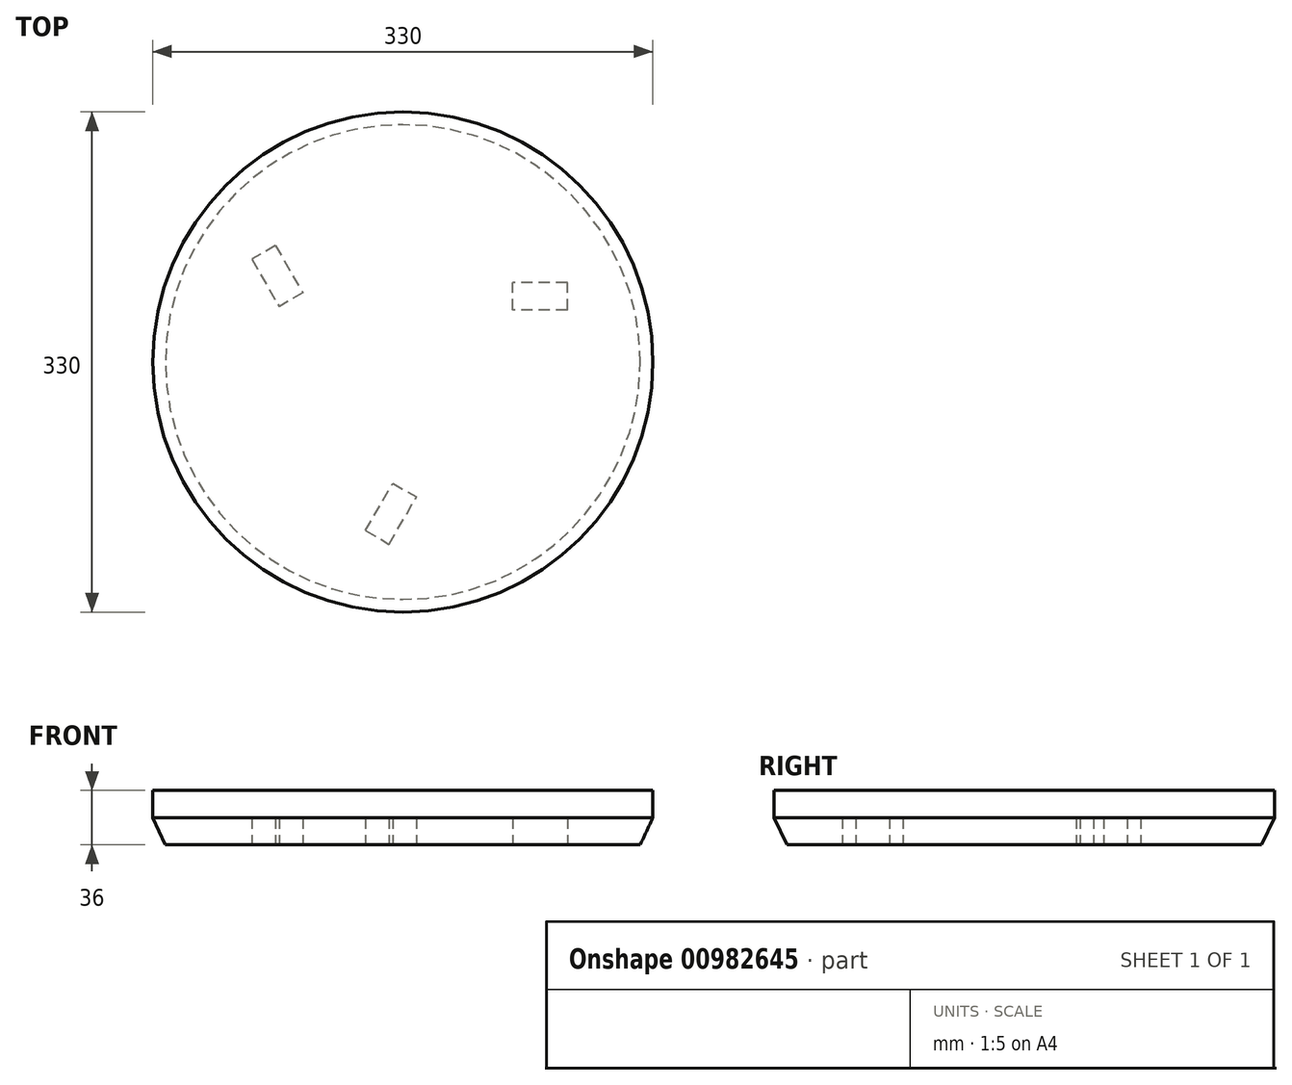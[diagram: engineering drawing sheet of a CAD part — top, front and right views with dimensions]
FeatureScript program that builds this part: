
annotation { "Feature Type Name" : "Feature", "Feature Type Description" : "" }
export const myFeature = defineFeature(function(context is Context, id is Id, definition is map)
    precondition{}
    {
        {
            var Q0;
            Q0=qCreatedBy(makeId("Top.planeOp"),FACE);
            var sketch = newSketch(context, id + "F0", { "sketchPlane" : qUnion([Q0])});
            skCircle(sketch, "E0", {"center": v(0, 0) * mm, "radius": 165 * mm});
            skSolve(sketch);
        }
        {
            var Q0;
            Q0=makeQuery(id+"F0.imprint","IMPRINT",FACE,{"disambiguationData":[TD([[makeQuery(id+"F0.imprint","IMPRINT",EDGE,{"derivedFrom":sQuery(id+"F0.wireOp",EDGE,"E0")}),1.0]])]});
            extrude(context, id + "F1", {"entities" : qUnion([Q0]), "depth" : 36 * mm, "offsetDistance" : 25 * mm});
        }
        {
            var Q0;
            Q0=makeQuery(id+"F1.opExtrude","CAP_FACE",FACE,{"disambiguationData":[OSD([sQuery(id+"F0.wireOp",EDGE,"E0")])],"isStart":true});
            var sketch = newSketch(context, id + "F2", { "sketchPlane" : qUnion([Q0])});
            skLineSegment(sketch, "E1.bottom", {"start": v(-24.59, 111.18) * mm, "end": v(-9, 120.18) * mm});
            skLineSegment(sketch, "E1.top", {"start": v(-6.59, 80) * mm, "end": v(9, 89) * mm});
            skLineSegment(sketch, "E1.left", {"start": v(-24.59, 111.18) * mm, "end": v(-6.59, 80) * mm});
            skLineSegment(sketch, "E1.right", {"start": v(-9, 120.18) * mm, "end": v(9, 89) * mm});
            skLineSegment(sketch, "E2", {"start": v(0, 0) * mm, "end": v(0, 83.8) * mm, "construction": true});
            skLineSegment(sketch, "E3.1.0", {"start": v(-99.58, -67.88) * mm, "end": v(-81.58, -36.7) * mm});
            skLineSegment(sketch, "E3.1.1", {"start": v(-83.99, -76.88) * mm, "end": v(-99.58, -67.88) * mm});
            skLineSegment(sketch, "E3.1.2", {"start": v(-83.99, -76.88) * mm, "end": v(-65.99, -45.7) * mm});
            skLineSegment(sketch, "E3.1.3", {"start": v(-65.99, -45.7) * mm, "end": v(-81.58, -36.7) * mm});
            skLineSegment(sketch, "E3.2.0", {"start": v(108.58, -52.3) * mm, "end": v(72.58, -52.3) * mm});
            skLineSegment(sketch, "E3.2.1", {"start": v(108.58, -34.3) * mm, "end": v(108.58, -52.3) * mm});
            skLineSegment(sketch, "E3.2.2", {"start": v(108.58, -34.3) * mm, "end": v(72.58, -34.3) * mm});
            skLineSegment(sketch, "E3.2.3", {"start": v(72.58, -34.3) * mm, "end": v(72.58, -52.3) * mm});
            skPoint(sketch, "E3.center", {"position": v(0, 0) * mm});
            skSolve(sketch);
        }
        {
            var Q0;
            Q0=makeQuery(id+"F2.imprint","IMPRINT",FACE,{"disambiguationData":[TD([[makeQuery(id+"F2.imprint","IMPRINT",EDGE,{"derivedFrom":sQuery(id+"F2.wireOp",EDGE,"E1.bottom")}),-1.0]])]});
            var Q1;
            Q1=makeQuery(id+"F2.imprint","IMPRINT",FACE,{"disambiguationData":[TD([[makeQuery(id+"F2.imprint","IMPRINT",EDGE,{"derivedFrom":sQuery(id+"F2.wireOp",EDGE,"E3.2.0")}),-1.0]])]});
            var Q2;
            Q2=makeQuery(id+"F2.imprint","IMPRINT",FACE,{"disambiguationData":[TD([[makeQuery(id+"F2.imprint","IMPRINT",EDGE,{"derivedFrom":sQuery(id+"F2.wireOp",EDGE,"E3.1.0")}),-1.0]])]});
            extrude(context, id + "F3", {"entities" : qUnion([Q0, Q1, Q2]), "operationType" : NewBodyOperationType.REMOVE, "oppositeDirection" : true, "depth" : 18 * mm, "offsetDistance" : 25 * mm});
        }
        {
            var Q0;
            Q0=makeQuery(id+"F1.opExtrude","CAP_EDGE",EDGE,{"disambiguationData":[OSD([sQuery(id+"F0.wireOp",EDGE,"E0")])],"isStart":true});
            chamfer(context, id + "F4", {"entities" : qUnion([Q0]), "chamferType" : ChamferType.OFFSET_ANGLE, "width" : 18 * mm, "oppositeDirection" : false, "angle" : 25 * degree, "tangentPropagation" : true});
        }
    });
